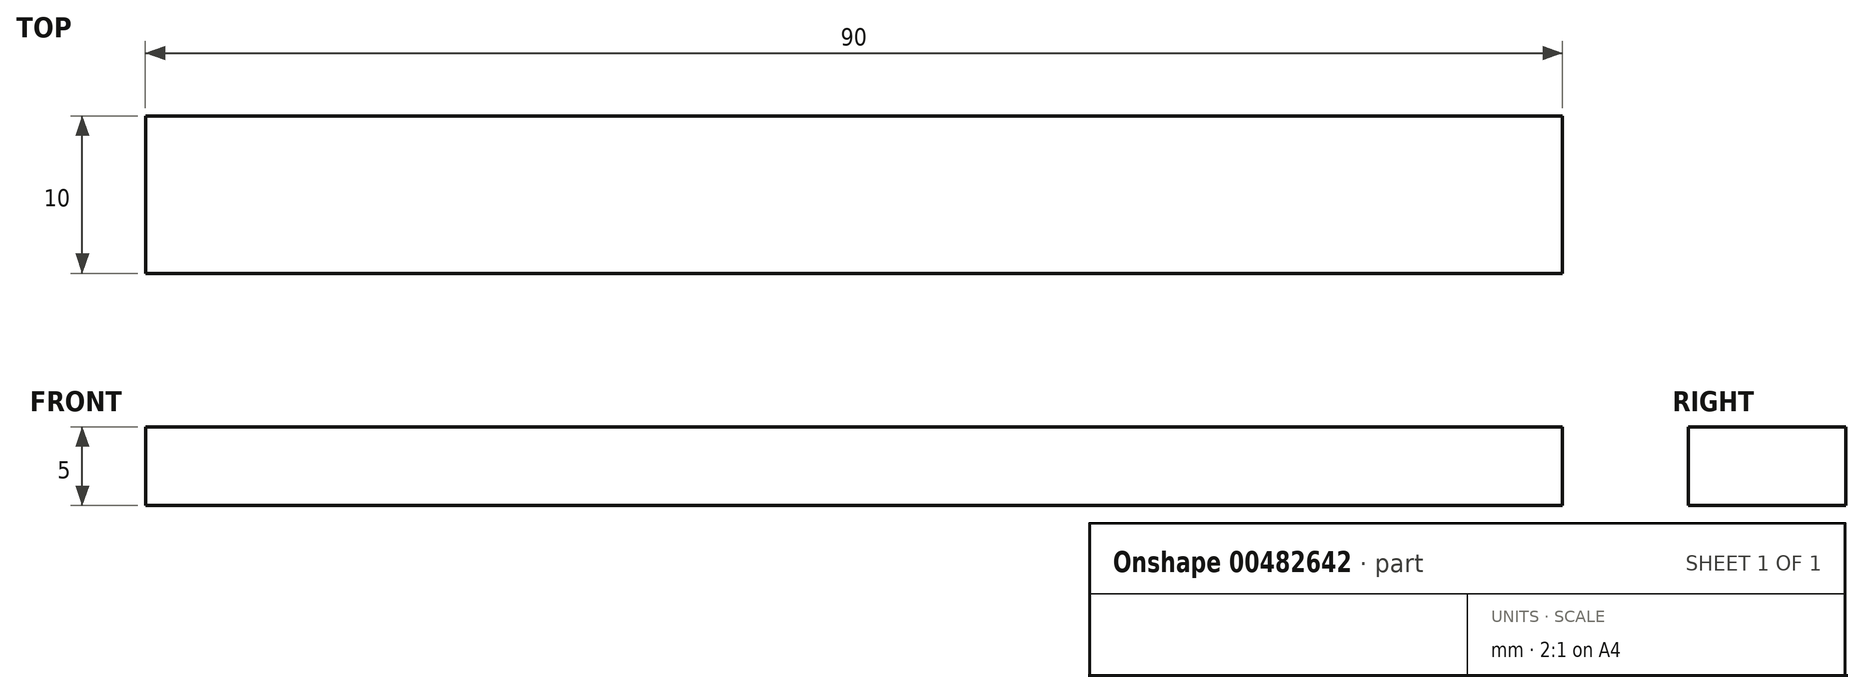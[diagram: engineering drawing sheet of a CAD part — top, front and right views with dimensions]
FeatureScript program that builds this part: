
annotation { "Feature Type Name" : "Feature", "Feature Type Description" : "" }
export const myFeature = defineFeature(function(context is Context, id is Id, definition is map)
    precondition{}
    {
        {
            var Q0;
            Q0=qCreatedBy(makeId("Top.planeOp"),FACE);
            var sketch = newSketch(context, id + "F0", { "sketchPlane" : qUnion([Q0])});
            skLineSegment(sketch, "E0.bottom", {"start": v(-31.68, 18.08) * mm, "end": v(58.32, 18.08) * mm});
            skLineSegment(sketch, "E0.top", {"start": v(-31.68, 8.08) * mm, "end": v(58.32, 8.08) * mm});
            skLineSegment(sketch, "E0.left", {"start": v(-31.68, 18.08) * mm, "end": v(-31.68, 8.08) * mm});
            skLineSegment(sketch, "E0.right", {"start": v(58.32, 18.08) * mm, "end": v(58.32, 8.08) * mm});
            skSolve(sketch);
        }
        {
            var Q0;
            Q0=makeQuery(id+"F0.imprint","IMPRINT",FACE,{"disambiguationData":[TD([[makeQuery(id+"F0.imprint","IMPRINT",EDGE,{"derivedFrom":sQuery(id+"F0.wireOp",EDGE,"E0.bottom")}),-1.0]])]});
            extrude(context, id + "F1", {"entities" : qUnion([Q0]), "depth" : 5 * mm});
        }
    });
